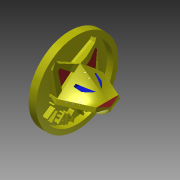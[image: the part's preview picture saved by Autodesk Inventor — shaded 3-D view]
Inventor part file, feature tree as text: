
AUTODESK INVENTOR PART (.ipt)
format: ipt  version: 2014 (Build 180170000, 170)  size: 1,013,760 bytes
history: native  units: in
note: dims shown in document units (in); Inventor stores cm internally (conversion verified against a paired STEP export)
features: sketch x21, extrude x14, plane x9, projected_geometry x5, loft x4, other x3, mirror x1, emboss x1
ambient origin geometry x8: Origin, YZ Plane, XZ Plane, XY Plane, X Axis, Y Axis, Z Axis, Center Point
bodies: Solid1 (feature_tree)
feature tree (58):
  sketch  "Sketch1"  dims[d0=0.7559in d1=0.7559in]
  plane  "Work Plane1"
  loft  "Loft1"
  extrude  "Extrusion1"  Depth=0.2in
  plane  "Work Plane4"
  loft  "Loft2"
  plane  "Work Plane5"
  loft  "Loft3"
  loft  "Loft4"
  extrude  "Extrusion2"  TaperAngle=0.0deg  [1 undecoded]
  plane  "Work Plane6"
  extrude  "Extrusion3"  Depth=1.0in
  extrude  "Extrusion4"  Depth=1.0651in
  extrude  "Extrusion5"  Depth=0.962in
  plane  "Work Plane7"
  extrude  "Extrusion6"  Depth=0.075in
  plane  "Work Plane8"
  other  "Work Axis1"
  plane  "Work Plane9"
  extrude  "Extrusion7"  Depth=0.06in
  mirror  "Mirror3"
  extrude  "Extrusion8"  Depth=0.05in
  plane  "Work Plane10"
  extrude  "Extrusion9"  Depth=0.0625in
  plane  "Work Plane11"
  extrude  "Extrusion10"  Depth=0.075in
  extrude  "Extrusion11"  TaperAngle=0.0deg  [1 undecoded]
  extrude  "Extrusion12"  Depth=0.2in
  extrude  "Extrusion13"  TaperAngle=0.0deg  [1 undecoded]
  emboss  "Emboss1"
  extrude  "Extrusion15"  Depth=0.01in
  sketch  "Sketch2"  dims[d2=0.9963in d3=0.2in]
  sketch  "Sketch3"  dims[d4=0.5in d6=0.08in]
  sketch  "Sketch4"  dims[d7=0.55in d8=150.0deg]
  other  "Edges1"
  sketch  "Sketch5"  dims[d9=150.0deg d14=0.33in]
  projected_geometry  "Projected Loop1"
  other  "Edges2"
  sketch  "Sketch6"  dims[d15=0.66in d18=0.0in d19=90.0deg]
  sketch  "Sketch7"  dims[d20=0.0in d21=90.0deg d22=1.0in]
  sketch  "Sketch8"  dims[d26=1.0651in d28=1.0651in]
  sketch  "Sketch9"  dims[d29=0.0in d30=0.962in]
  sketch  "Sketch10"  dims[d31=0.962in d32=0.075in]
  sketch  "Sketch11"  dims[d33=0.15in d34=0.06in]
  sketch  "Sketch12"  dims[d35=0.1in d36=0.05in]
  sketch  "Sketch13"  dims[d37=0.45in d38=0.0in d39=0.0625in]
  projected_geometry  "Projected Loop2"
  projected_geometry  "Projected Loop3"
  sketch  "Sketch14"  dims[d40=0.01in d41=0.075in]
  projected_geometry  "Projected Loop4"
  sketch  "Sketch15"  dims[d42=0.01in d43=0.0in d44=90.0deg]
  sketch  "Sketch16"  dims[d45=0.0in d46=90.0deg d47=0.2in]
  sketch  "Sketch17"  dims[d48=0.07in d49=0.0in d50=90.0deg]
  sketch  "Sketch18"  dims[d51=0.0in d52=90.0deg d53=0.01in]
  sketch  "Sketch19"  dims[d54=0.01in]
  sketch  "Sketch20"  dims[d55=0.0344in]
  sketch  "Sketch22"  dims[d56=150.0deg d57=60.0deg d58=150.0deg d59=0.7in d60=0.05in d61=0.05in d62=0.05in d63=0.05in d64=0.05in d65=0.01in d66=0.0in d67=90.0deg d68=0.0in d69=90.0deg d70=0.1in d71=0.4in d72=0.15in d73=0.05in d74=0.0in d75=0.02in d77=0.15in d78=0.02in d79=0.1in d80=0.1in d81=0.1in d82=0.02in d83=0.15in d84=0.05in d85=0.0in d86=0.045in d87=0.0in d88=0.025in d89=0.0in d90=0.02in d91=0.02in d92=0.005in d93=0.0in d94=90.0deg d95=0.4466in d96=1.0in d97=0.0in d98=1.0in d99=0.0in d100=0.6528in d101=0.0in d102=0.0in d103=1.0in d104=0.0in d106=90.0deg d107=1.0in d108=0.0in d109=1.65in d110=0.1in d111=0.075in d112=0.0in d113=0.1in d114=0.075in d115=0.0in d116=0.05in d117=0.0in d121=0.05in d122=0.0in]
  projected_geometry  "Projected Loop5"
note: 3 required parameter values undecoded (feature->parameter linkage not recoverable at this tier; creation-order binding heuristic only, values carry confidence <= 0.55)
